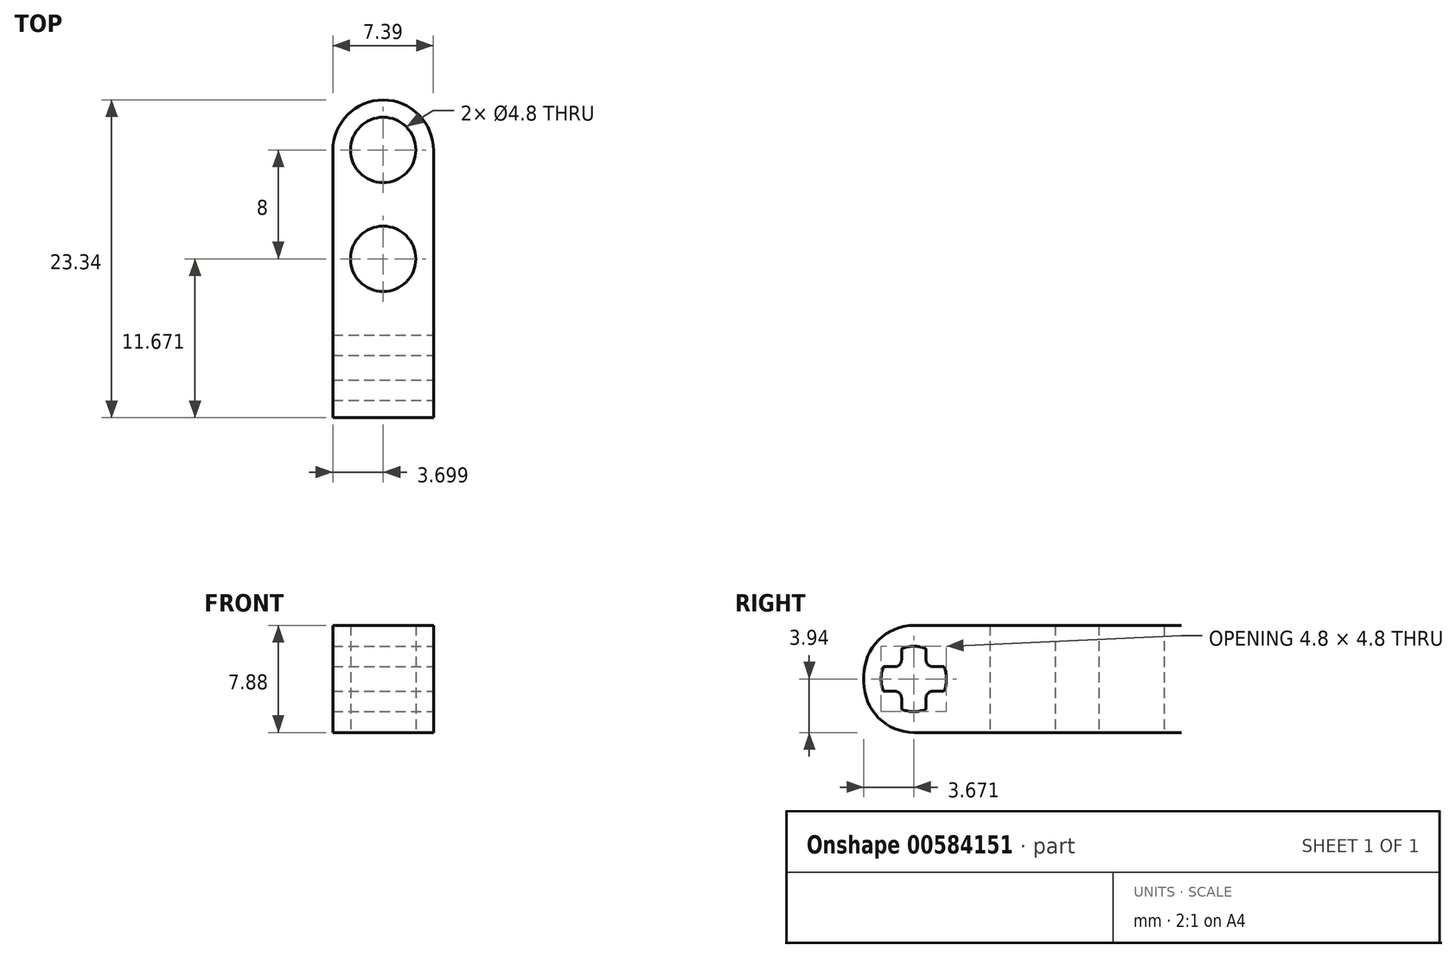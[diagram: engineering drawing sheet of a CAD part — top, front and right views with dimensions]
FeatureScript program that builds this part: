
annotation { "Feature Type Name" : "Feature", "Feature Type Description" : "" }
export const myFeature = defineFeature(function(context is Context, id is Id, definition is map)
    precondition{}
    {
        {
            var Q0;
            Q0=qCreatedBy(makeId("Top.planeOp"),FACE);
            var sketch = newSketch(context, id + "F0", { "sketchPlane" : qUnion([Q0])});
            skLineSegment(sketch, "E0.bottom", {"start": v(-64.8, -20.3) * mm, "end": v(-57.4, -20.3) * mm});
            skLineSegment(sketch, "E0.top", {"start": v(-64.8, 3.04) * mm, "end": v(-57.4, 3.04) * mm});
            skLineSegment(sketch, "E0.left", {"start": v(-64.8, -20.3) * mm, "end": v(-64.8, 3.04) * mm});
            skLineSegment(sketch, "E0.right", {"start": v(-57.4, -20.3) * mm, "end": v(-57.4, 3.04) * mm});
            skLineSegment(sketch, "E1", {"start": v(-66.28, -8.63) * mm, "end": v(-56.38, -8.63) * mm, "construction": true});
            skPoint(sketch, "E1.startSnap0", {"position": v(-64.8, -8.63) * mm});
            skPoint(sketch, "E1.endSnap0", {"position": v(-57.4, -8.63) * mm});
            skCircle(sketch, "E2", {"center": v(-61.1, -8.63) * mm, "radius": 2.4 * mm});
            skPoint(sketch, "E2.centerSnap0", {"position": v(-61.1, -20.3) * mm});
            skCircle(sketch, "E3.0.1.0", {"center": v(-61.1, -0.63) * mm, "radius": 2.4 * mm});
            skLineSegment(sketch, "E3.direction1", {"start": v(-61.1, -8.63) * mm, "end": v(-51.5, -8.4) * mm, "construction": true});
            skLineSegment(sketch, "E3.direction2", {"start": v(-61.1, -8.63) * mm, "end": v(-61.1, -0.63) * mm, "construction": true});
            skSolve(sketch);
        }
        {
            var Q0;
            Q0=makeQuery(id+"F0.imprint","IMPRINT",FACE,{"disambiguationData":[TD([[makeQuery(id+"F0.imprint","IMPRINT",EDGE,{"derivedFrom":sQuery(id+"F0.wireOp",EDGE,"E0.bottom")}),1.0]])]});
            extrude(context, id + "F1", {"entities" : qUnion([Q0]), "depth" : 7.88 * mm, "offsetDistance" : 25 * mm});
        }
        {
            var Q0;
            Q0=makeQuery(id+"F1.opExtrude","SWEPT_EDGE",EDGE,{"disambiguationData":[OSD([sQuery(id+"F0.wireOp",EDGE,"E0.top"),sQuery(id+"F0.wireOp",EDGE,"E0.left")])]});
            var Q1;
            Q1=makeQuery(id+"F1.opExtrude","SWEPT_EDGE",EDGE,{"disambiguationData":[OSD([sQuery(id+"F0.wireOp",EDGE,"E0.top"),sQuery(id+"F0.wireOp",EDGE,"E0.right")])]});
            fillet(context, id + "F2", {"entities" : qUnion([Q0, Q1]), "radius" : 3.7 * mm, "tangentPropagation" : true, "allowEdgeOverflow" : false});
        }
        {
            var Q0;
            Q0=makeQuery(id+"F1.opExtrude","SWEPT_FACE",FACE,{"disambiguationData":[OSD([sQuery(id+"F0.wireOp",EDGE,"E0.right")])]});
            var sketch = newSketch(context, id + "F3", { "sketchPlane" : qUnion([Q0])});
            skLineSegment(sketch, "E4.0", {"start": v(-11.03, 7.88) * mm, "end": v(-6.23, 7.88) * mm, "construction": true});
            skLineSegment(sketch, "E5.0", {"start": v(-20.3, 7.88) * mm, "end": v(-20.3, 0) * mm, "construction": true});
            skLineSegment(sketch, "E6.1", {"start": v(3.04, 7.88) * mm, "end": v(3.04, 0) * mm, "construction": true});
            skPoint(sketch, "E7", {"position": v(-8.63, 3.94) * mm});
            skPoint(sketch, "E7.positionSnap0", {"position": v(-8.63, 7.88) * mm});
            skPoint(sketch, "E7.positionSnap1", {"position": v(-13.7, 4.52) * mm});
            skLineSegment(sketch, "E8", {"start": v(-22.31, 3.94) * mm, "end": v(-10.48, 3.94) * mm, "construction": true});
            skArc(sketch, "E9.MirrorCS", {"start": v(-15.73, 6.1) * mm, "mid": v(-15.75, 6.15) * mm, "end": v(-15.8, 6.2) * mm});
            skArc(sketch, "E10.MirrorCS", {"start": v(-17.46, 6.2) * mm, "mid": v(-17.51, 6.15) * mm, "end": v(-17.53, 6.1) * mm});
            skArc(sketch, "E11.MirrorCS", {"start": v(-18.79, 4.84) * mm, "mid": v(-18.84, 4.82) * mm, "end": v(-18.88, 4.77) * mm});
            skArc(sketch, "E12.MirrorCS", {"start": v(-14.38, 4.77) * mm, "mid": v(-14.42, 4.82) * mm, "end": v(-14.47, 4.84) * mm});
            skPoint(sketch, "E13.MirrorP", {"position": v(-14.23, 3.94) * mm});
            skArc(sketch, "E14.MirrorCS", {"start": v(-14.23, 3.94) * mm, "mid": v(-14.27, 4.36) * mm, "end": v(-14.38, 4.77) * mm});
            skLineSegment(sketch, "E15.MirrorCS", {"start": v(-15.73, 5.34) * mm, "end": v(-15.73, 6.1) * mm});
            skArc(sketch, "E16.MirrorCS", {"start": v(-15.8, 6.2) * mm, "mid": v(-16.63, 6.34) * mm, "end": v(-17.46, 6.2) * mm});
            skLineSegment(sketch, "E17.MirrorCS", {"start": v(-17.53, 6.1) * mm, "end": v(-17.53, 5.34) * mm});
            skArc(sketch, "E18.MirrorCS", {"start": v(-17.53, 5.34) * mm, "mid": v(-17.68, 4.99) * mm, "end": v(-18.03, 4.84) * mm});
            skLineSegment(sketch, "E19.MirrorCS", {"start": v(-18.03, 4.84) * mm, "end": v(-18.79, 4.84) * mm});
            skArc(sketch, "E20.MirrorCS", {"start": v(-15.23, 4.84) * mm, "mid": v(-15.58, 4.99) * mm, "end": v(-15.73, 5.34) * mm});
            skLineSegment(sketch, "E21.MirrorCS", {"start": v(-14.47, 4.84) * mm, "end": v(-15.23, 4.84) * mm});
            skArc(sketch, "E22.MirrorCS", {"start": v(-18.88, 4.77) * mm, "mid": v(-19, 4.36) * mm, "end": v(-19.03, 3.94) * mm});
            skArc(sketch, "E23.MirrorCS", {"start": v(-18.79, 3.04) * mm, "mid": v(-18.84, 3.06) * mm, "end": v(-18.88, 3.1) * mm});
            skArc(sketch, "E24.MirrorCS", {"start": v(-14.38, 3.1) * mm, "mid": v(-14.42, 3.06) * mm, "end": v(-14.47, 3.04) * mm});
            skArc(sketch, "E25.MirrorCS", {"start": v(-15.73, 1.78) * mm, "mid": v(-15.75, 1.73) * mm, "end": v(-15.8, 1.69) * mm});
            skArc(sketch, "E26.MirrorCS", {"start": v(-17.46, 1.69) * mm, "mid": v(-17.51, 1.73) * mm, "end": v(-17.53, 1.78) * mm});
            skLineSegment(sketch, "E27.MirrorCS", {"start": v(-14.47, 3.04) * mm, "end": v(-15.23, 3.04) * mm});
            skArc(sketch, "E28.MirrorCS", {"start": v(-14.23, 3.94) * mm, "mid": v(-14.27, 3.52) * mm, "end": v(-14.38, 3.1) * mm});
            skPoint(sketch, "E29.MirrorP", {"position": v(-13.7, 3.36) * mm});
            skLineSegment(sketch, "E30.MirrorCS", {"start": v(-15.73, 2.54) * mm, "end": v(-15.73, 1.78) * mm});
            skLineSegment(sketch, "E31.MirrorCS", {"start": v(-17.53, 1.78) * mm, "end": v(-17.53, 2.54) * mm});
            skLineSegment(sketch, "E32.MirrorCS", {"start": v(-18.03, 3.04) * mm, "end": v(-18.79, 3.04) * mm});
            skArc(sketch, "E33.MirrorCS", {"start": v(-18.88, 3.1) * mm, "mid": v(-19, 3.52) * mm, "end": v(-19.03, 3.94) * mm});
            skArc(sketch, "E34.MirrorCS", {"start": v(-15.8, 1.69) * mm, "mid": v(-16.63, 1.54) * mm, "end": v(-17.46, 1.69) * mm});
            skArc(sketch, "E35.MirrorCS", {"start": v(-15.23, 3.04) * mm, "mid": v(-15.58, 2.9) * mm, "end": v(-15.73, 2.54) * mm});
            skArc(sketch, "E36.MirrorCS", {"start": v(-17.53, 2.54) * mm, "mid": v(-17.68, 2.9) * mm, "end": v(-18.03, 3.04) * mm});
            skSolve(sketch);
        }
        {
            var Q0;
            Q0=makeQuery(id+"F3.imprint","IMPRINT",FACE,{"disambiguationData":[TD([[makeQuery(id+"F3.imprint","IMPRINT",EDGE,{"derivedFrom":sQuery(id+"F3.wireOp",EDGE,"E9.MirrorCS")}),1.0]])]});
            extrude(context, id + "F4", {"entities" : qUnion([Q0]), "operationType" : NewBodyOperationType.REMOVE, "endBound" : BoundingType.THROUGH_ALL, "oppositeDirection" : true, "depth" : 25 * mm, "offsetDistance" : 25 * mm});
        }
        {
            var Q0;
            Q0=makeQuery(id+"F1.opExtrude","CAP_EDGE",EDGE,{"disambiguationData":[OSD([sQuery(id+"F0.wireOp",EDGE,"E0.bottom")])],"isStart":false});
            var Q1;
            Q1=makeQuery(id+"F1.opExtrude","CAP_EDGE",EDGE,{"disambiguationData":[OSD([sQuery(id+"F0.wireOp",EDGE,"E0.bottom")])],"isStart":true});
            fillet(context, id + "F5", {"entities" : qUnion([Q0, Q1]), "radius" : 3.7 * mm, "tangentPropagation" : true, "allowEdgeOverflow" : false});
        }
    });
